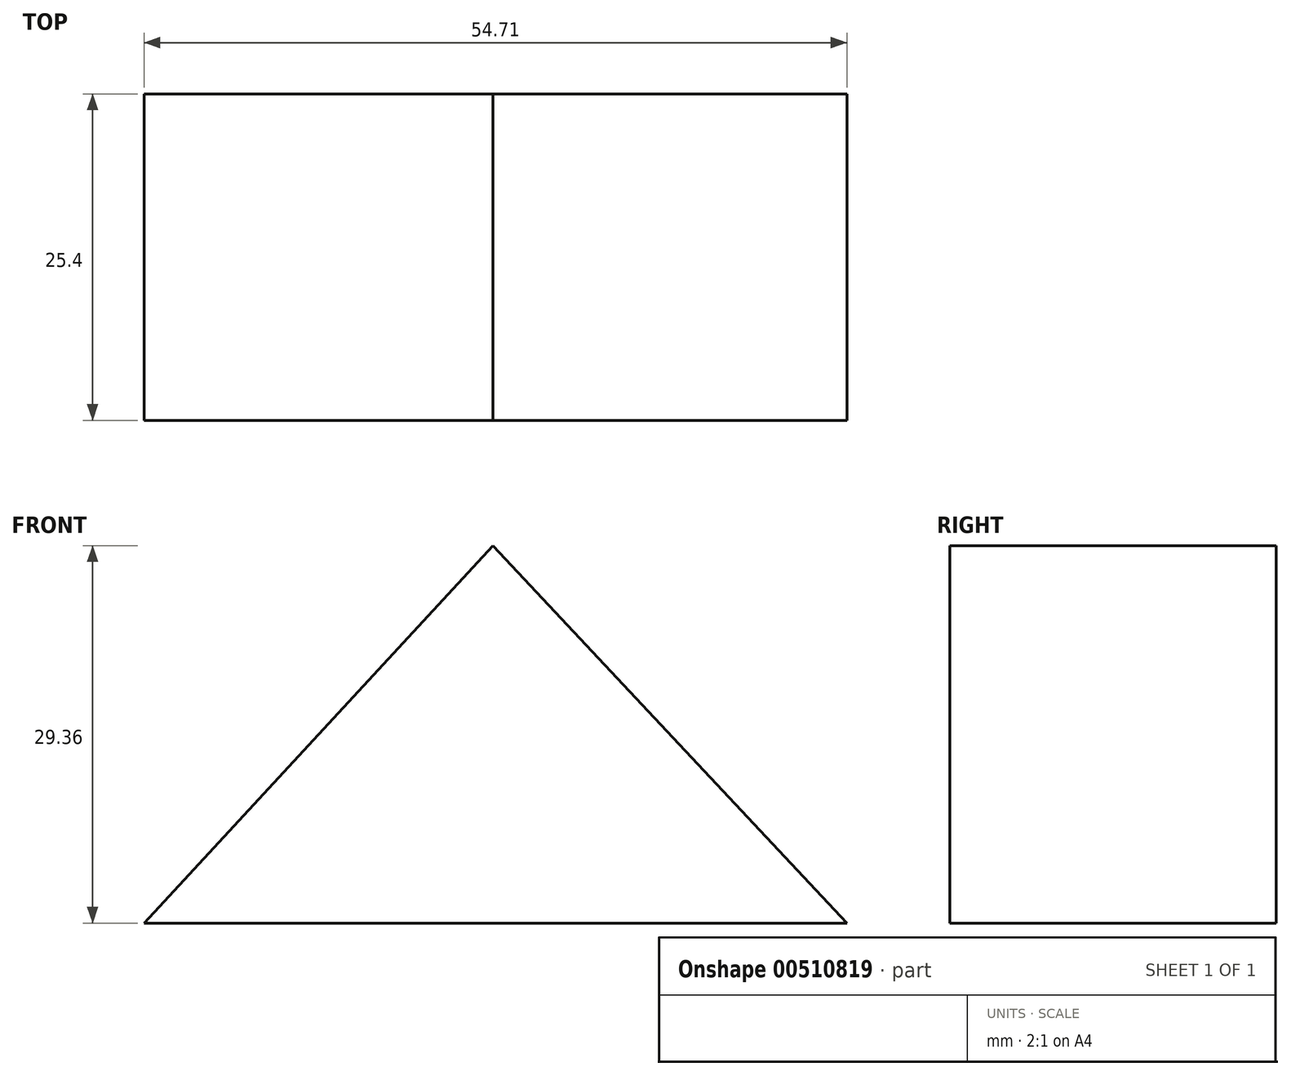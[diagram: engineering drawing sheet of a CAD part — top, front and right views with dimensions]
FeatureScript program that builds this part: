
annotation { "Feature Type Name" : "Feature", "Feature Type Description" : "" }
export const myFeature = defineFeature(function(context is Context, id is Id, definition is map)
    precondition{}
    {
        {
            var Q0;
            Q0=qCreatedBy(makeId("Front.planeOp"),FACE);
            var sketch = newSketch(context, id + "F0", { "sketchPlane" : qUnion([Q0])});
            skLineSegment(sketch, "E0", {"start": v(-27.17, 17.47) * mm, "end": v(27.54, 17.47) * mm});
            skLineSegment(sketch, "E1", {"start": v(27.54, 17.47) * mm, "end": v(0, 46.83) * mm});
            skLineSegment(sketch, "E2", {"start": v(0, 46.83) * mm, "end": v(-27.17, 17.47) * mm});
            skSolve(sketch);
        }
        {
            var Q0;
            Q0=makeQuery(id+"F0.imprint","IMPRINT",FACE,{"disambiguationData":[TD([[makeQuery(id+"F0.imprint","IMPRINT",EDGE,{"derivedFrom":sQuery(id+"F0.wireOp",EDGE,"E0")}),1.0]])]});
            extrude(context, id + "F1", {"entities" : qUnion([Q0]), "depth" : 25.4 * mm});
        }
    });
